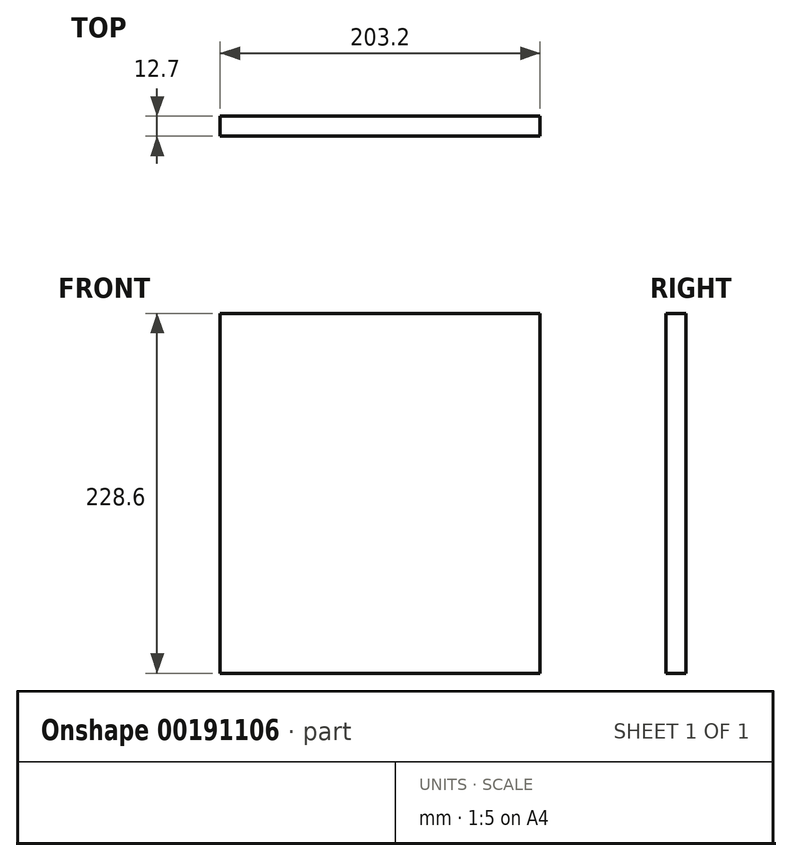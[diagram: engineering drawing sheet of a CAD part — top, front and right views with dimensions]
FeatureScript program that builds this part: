
annotation { "Feature Type Name" : "Feature", "Feature Type Description" : "" }
export const myFeature = defineFeature(function(context is Context, id is Id, definition is map)
    precondition{}
    {
        {
            var Q0;
            Q0=qCreatedBy(makeId("Front.planeOp"),FACE);
            var sketch = newSketch(context, id + "F0", { "sketchPlane" : qUnion([Q0])});
            skLineSegment(sketch, "E0.bottom", {"start": v(101.6, 114.3) * mm, "end": v(-101.6, 114.3) * mm});
            skLineSegment(sketch, "E0.top", {"start": v(101.6, -114.3) * mm, "end": v(-101.6, -114.3) * mm});
            skLineSegment(sketch, "E0.left", {"start": v(101.6, 114.3) * mm, "end": v(101.6, -114.3) * mm});
            skLineSegment(sketch, "E0.right", {"start": v(-101.6, 114.3) * mm, "end": v(-101.6, -114.3) * mm});
            skPoint(sketch, "E0.middle", {"position": v(0, 0) * mm});
            skSolve(sketch);
        }
        {
            var Q0;
            Q0 = qSketchRegion(id + "F0", true);
            extrude(context, id + "F1", {"entities" : qUnion([Q0]), "depth" : 12.7 * mm});
        }
    });
